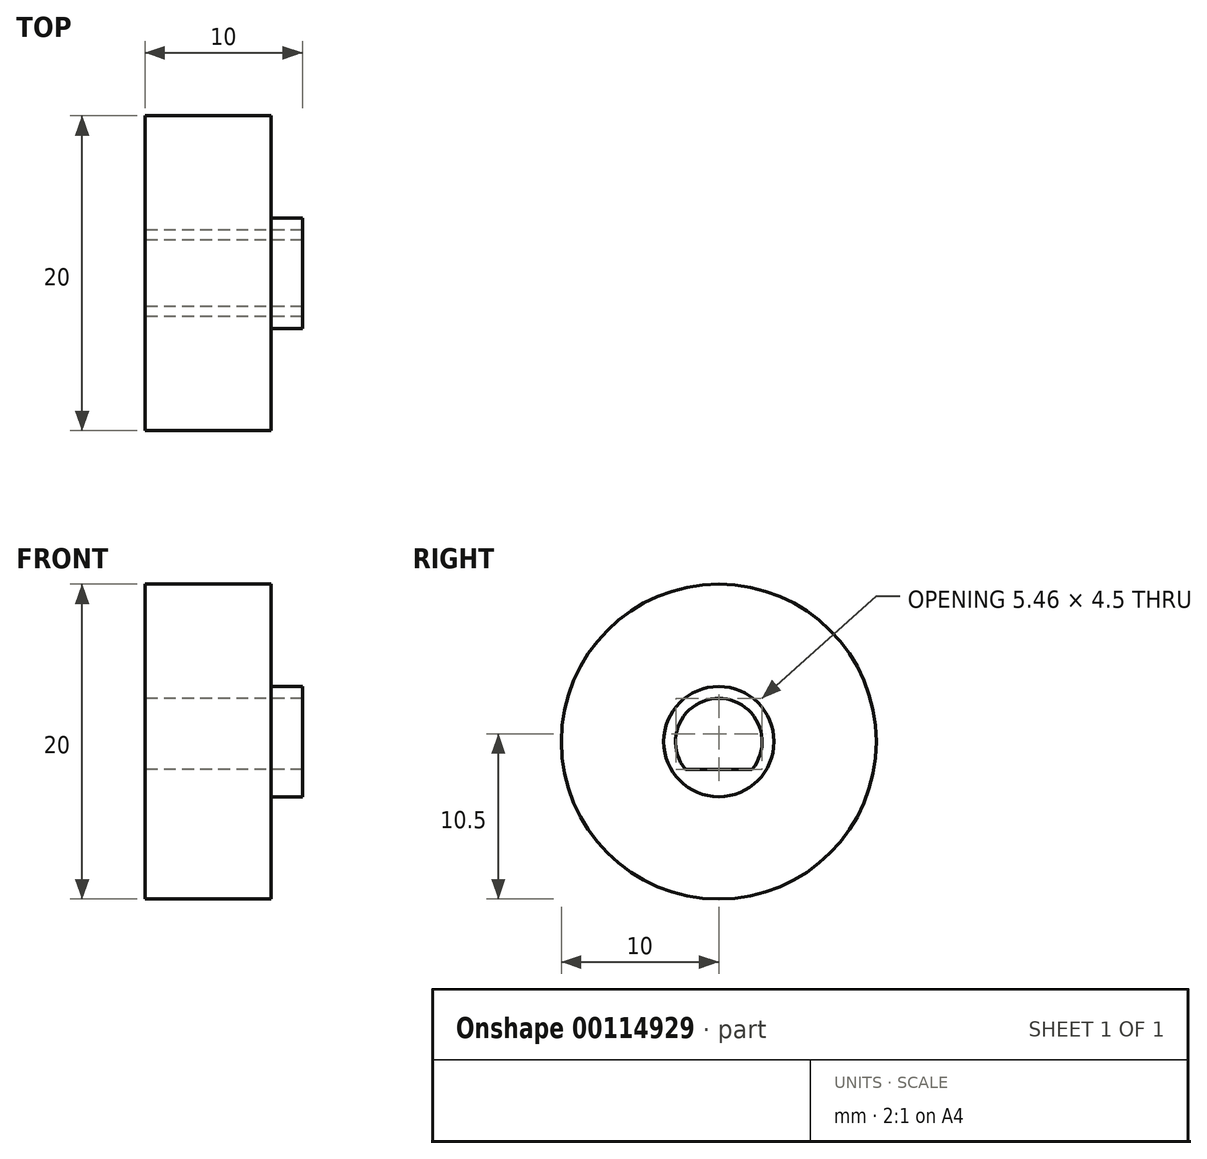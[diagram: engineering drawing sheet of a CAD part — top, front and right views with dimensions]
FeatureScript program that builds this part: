
annotation { "Feature Type Name" : "Feature", "Feature Type Description" : "" }
export const myFeature = defineFeature(function(context is Context, id is Id, definition is map)
    precondition{}
    {
        {
            var Q0;
            Q0=qCreatedBy(makeId("Right.planeOp"),FACE);
            var sketch = newSketch(context, id + "F0", { "sketchPlane" : qUnion([Q0])});
            skCircle(sketch, "E0", {"center": v(0, 0) * mm, "radius": 10 * mm});
            skArc(sketch, "E1", {"start": v(2.12, -1.75) * mm, "mid": v(0, 2.75) * mm, "end": v(-2.12, -1.75) * mm});
            skLineSegment(sketch, "E2", {"start": v(2.12, -1.75) * mm, "end": v(-2.12, -1.75) * mm});
            skSolve(sketch);
        }
        {
            var Q0;
            Q0=qSketchRegion(id+"F0",true);
            extrude(context, id + "F1", {"entities" : qUnion([Q0]), "depth" : 10 * mm});
        }
        {
            var Q0;
            Q0=makeQuery(id+"F1.opExtrude","CAP_FACE",FACE,{"disambiguationData":[OSD([sQuery(id+"F0.wireOp",EDGE,"E0"),sQuery(id+"F0.wireOp",EDGE,"E1"),sQuery(id+"F0.wireOp",EDGE,"E2")])],"isStart":false});
            var sketch = newSketch(context, id + "F2", { "sketchPlane" : qUnion([Q0])});
            skCircle(sketch, "E3", {"center": v(0, 0) * mm, "radius": 3.5 * mm});
            skSolve(sketch);
        }
        {
            var Q0;
            Q0=makeQuery(id+"F2.imprint","IMPRINT",FACE,{"disambiguationData":[TD([[makeQuery(id+"F2.imprint","IMPRINT",EDGE,{"derivedFrom":sQuery(id+"F2.wireOp",EDGE,"E3")}),-1.0]])]});
            extrude(context, id + "F3", {"entities" : qUnion([Q0]), "operationType" : NewBodyOperationType.REMOVE, "oppositeDirection" : true, "depth" : 2 * mm});
        }
    });
